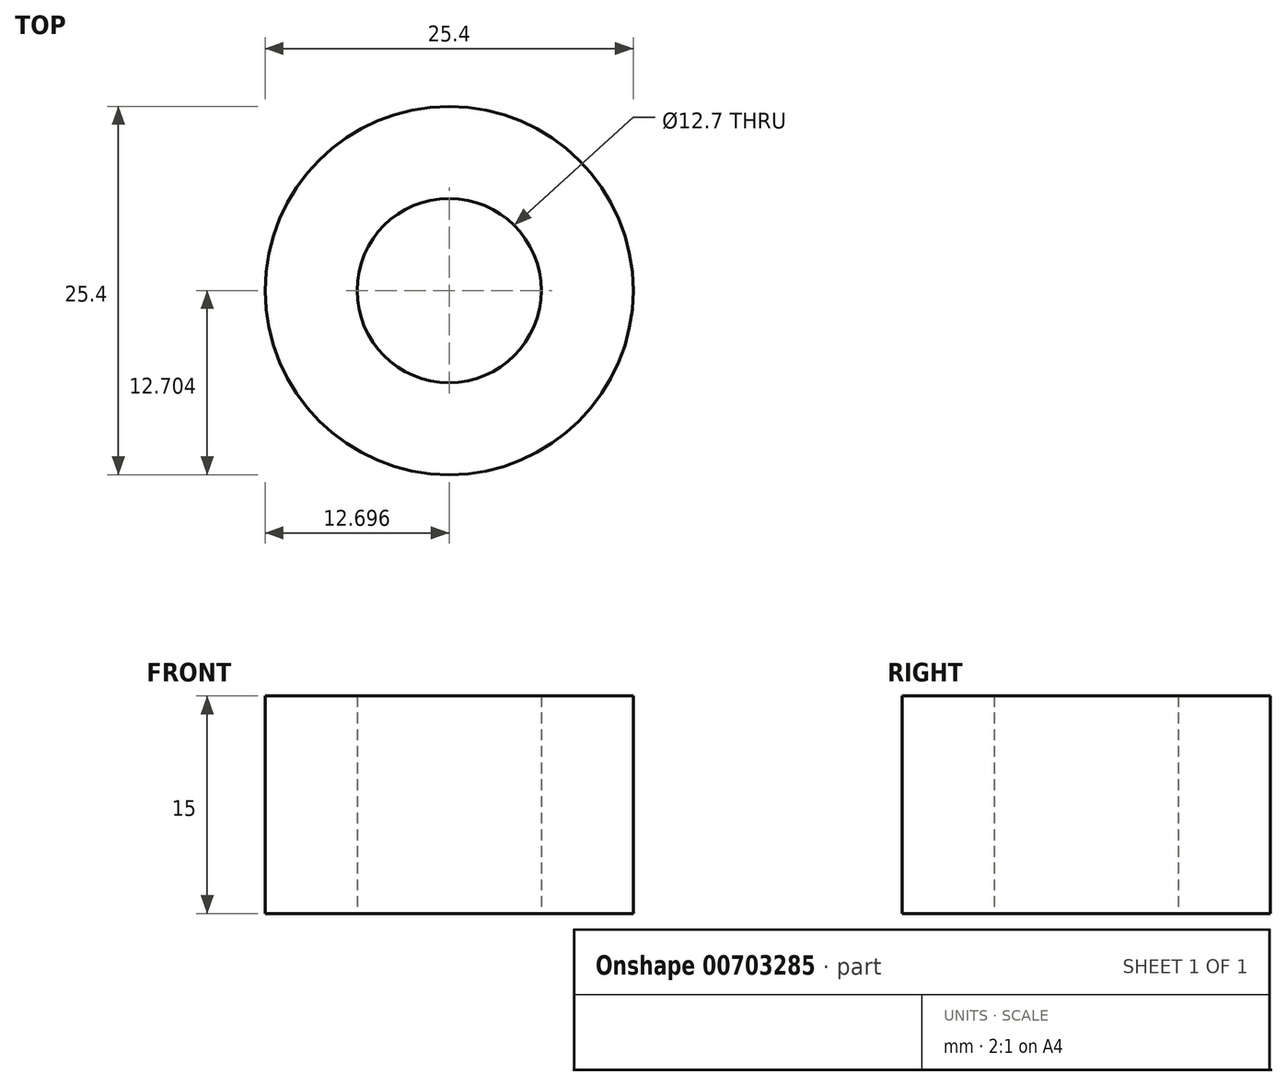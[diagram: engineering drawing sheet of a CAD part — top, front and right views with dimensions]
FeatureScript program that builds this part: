
annotation { "Feature Type Name" : "Feature", "Feature Type Description" : "" }
export const myFeature = defineFeature(function(context is Context, id is Id, definition is map)
    precondition{}
    {
        {
            var Q0;
            Q0=qCreatedBy(makeId("Top.planeOp"),FACE);
            var sketch = newSketch(context, id + "F0", { "sketchPlane" : qUnion([Q0])});
            skCircle(sketch, "E0", {"center": v(-144.61, -14.06) * mm, "radius": 12.7 * mm});
            skCircle(sketch, "E1", {"center": v(-144.61, -14.06) * mm, "radius": 6.35 * mm});
            skSolve(sketch);
        }
        {
            var Q0;
            Q0=makeQuery(id+"F0.imprint","IMPRINT",FACE,{"disambiguationData":[TD([[makeQuery(id+"F0.imprint","IMPRINT",EDGE,{"derivedFrom":sQuery(id+"F0.wireOp",EDGE,"E0")}),1.0]])]});
            extrude(context, id + "F1", {"entities" : qUnion([Q0]), "depth" : 15 * mm, "offsetDistance" : 25.4 * mm});
        }
    });
